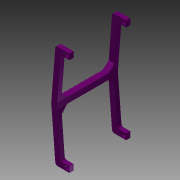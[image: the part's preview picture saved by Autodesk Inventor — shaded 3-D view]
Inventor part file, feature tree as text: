
AUTODESK INVENTOR PART (.ipt)
format: ipt  version: 2015 (Build 190159000, 159)  size: 374,272 bytes
history: native  units: mm
features: extrude x8, sketch x7, plane x2, mirror x2
ambient origin geometry x8: Origin, YZ Plane, XZ Plane, XY Plane, X Axis, Y Axis, Z Axis, Center Point
bodies: Body1 (feature_tree)
feature tree (19):
  extrude  "Extrusion11"  Depth=5.0mm
  extrude  "Extrusion12"  Depth=13.585143mm
  plane  "Work Plane10"
  extrude  "Extrusion13"  Depth=7.5mm
  plane  "Work Plane11"
  mirror  "Mirror5"
  mirror  "Mirror6"
  extrude  "Extrusion15"  Depth=2.0mm
  extrude  "Extrusion16"  Depth=5.0mm
  extrude  "Extrusion17"  Depth=22.75mm TaperAngle=0.0deg
  extrude  "Extrusion18"  Depth=5.0mm
  extrude  "Extrusion19"  TaperAngle=90.0deg  [1 undecoded]
  sketch  "Sketch1"  dims[d4=3.5mm d8=5.0mm]
  sketch  "Sketch5"  dims[d9=5.0mm d16=13.585143mm]
  sketch  "Sketch6"  dims[d20=2.5mm d62=7.5mm]
  sketch  "Sketch8"  dims[d63=2.5mm d64=2.0mm]
  sketch  "Sketch9"  dims[d65=3.5mm d66=0.0mm d67=5.0mm]
  sketch  "Sketch10"  dims[d68=5.0mm d69=22.75mm d70=0.0mm]
  sketch  "Sketch11"  dims[d71=-33.25mm d72=5.0mm d73=90.0deg d74=45.0deg d75=7.0mm d76=0.0mm d77=0.0mm d83=10.0mm d84=0.0mm d85=10.0mm d86=0.0mm d87=10.0mm d88=0.0mm d89=10.0mm d90=0.0mm d91=1.5mm d92=0.0mm]
note: 1 required parameter value undecoded (feature->parameter linkage not recoverable at this tier; creation-order binding heuristic only, values carry confidence <= 0.55)
